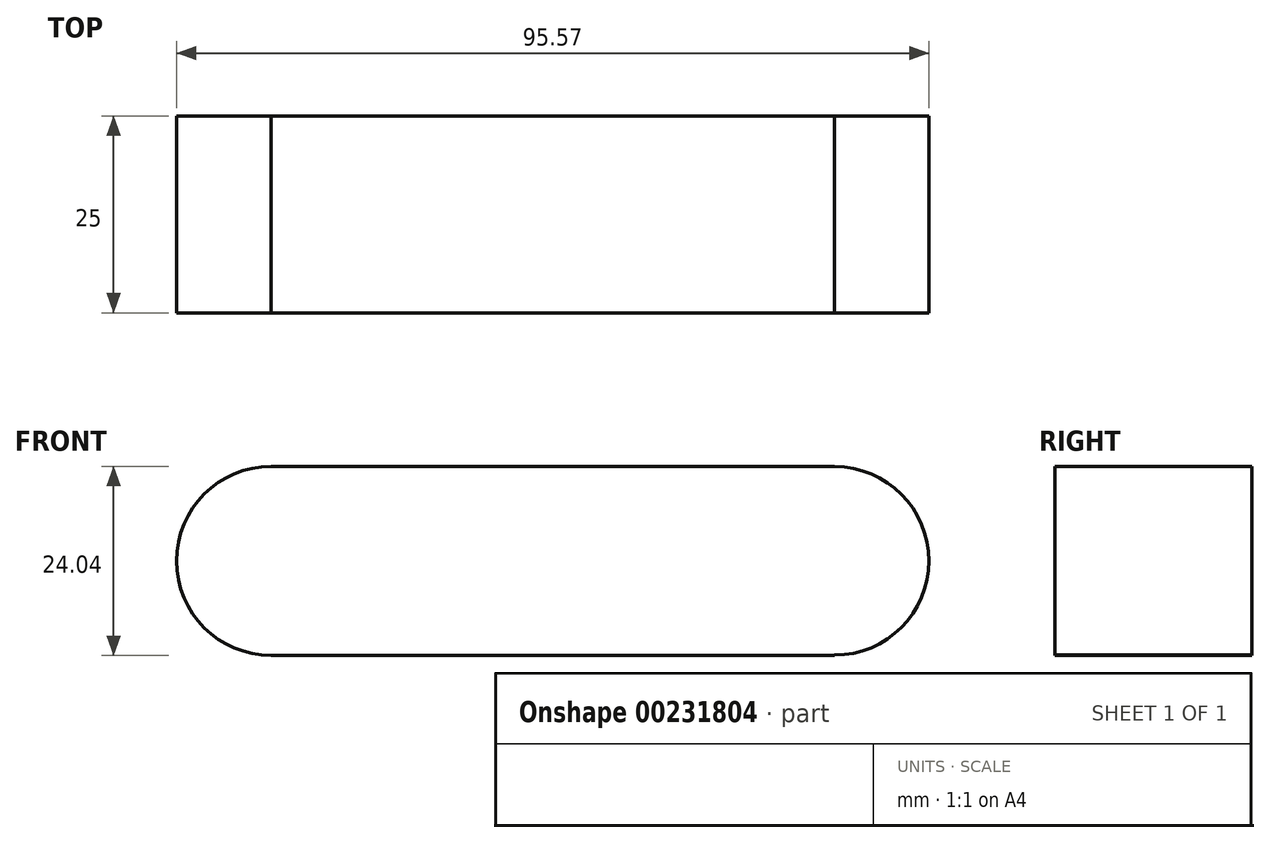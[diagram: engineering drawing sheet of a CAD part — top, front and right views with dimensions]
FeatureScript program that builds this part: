
annotation { "Feature Type Name" : "Feature", "Feature Type Description" : "" }
export const myFeature = defineFeature(function(context is Context, id is Id, definition is map)
    precondition{}
    {
        {
            var Q0;
            Q0=qCreatedBy(makeId("Front.planeOp"),FACE);
            var sketch = newSketch(context, id + "F0", { "sketchPlane" : qUnion([Q0])});
            skLineSegment(sketch, "E0.bottom", {"start": v(-35.8, 12.02) * mm, "end": v(35.8, 12.02) * mm});
            skLineSegment(sketch, "E0.top", {"start": v(-35.8, -12.02) * mm, "end": v(35.8, -12.02) * mm});
            skLineSegment(sketch, "E0.left", {"start": v(-35.8, 12.02) * mm, "end": v(-35.8, -12.02) * mm});
            skLineSegment(sketch, "E0.right", {"start": v(35.8, 12.02) * mm, "end": v(35.8, -12.02) * mm});
            skPoint(sketch, "E0.middle", {"position": v(0, 0) * mm});
            skArc(sketch, "E1", {"start": v(-35.8, 12) * mm, "mid": v(-47.8, 0) * mm, "end": v(-35.8, -12) * mm});
            skArc(sketch, "E2", {"start": v(35.8, -11.97) * mm, "mid": v(47.77, 0) * mm, "end": v(35.8, 11.97) * mm});
            skLineSegment(sketch, "E3", {"start": v(35.8, -12.02) * mm, "end": v(35.8, 12.02) * mm});
            skSolve(sketch);
        }
        {
            var Q0;
            {var subQ0=sQuery(id+"F0.wireOp",EDGE,"E1");Q0=makeQuery(id+"F0.imprint","IMPRINT",FACE,{"disambiguationData":[TD([[makeQuery(id+"F0.imprint","IMPRINT",EDGE,{"derivedFrom":subQ0}),1.0]])]});}
            var Q1;
            {var subQ4=sQuery(id+"F0.wireOp",EDGE,"E0.bottom");Q1=makeQuery(id+"F0.imprint","IMPRINT",FACE,{"disambiguationData":[TD([[makeQuery(id+"F0.imprint","IMPRINT",EDGE,{"derivedFrom":subQ4}),-1.0]])]});}
            var Q2;
            {var subQ0=sQuery(id+"F0.wireOp",EDGE,"E2");Q2=makeQuery(id+"F0.imprint","IMPRINT",FACE,{"disambiguationData":[TD([[makeQuery(id+"F0.imprint","IMPRINT",EDGE,{"derivedFrom":subQ0}),1.0]])]});}
            extrude(context, id + "F1", {"entities" : qUnion([Q0, Q1, Q2]), "depth" : 25 * mm});
        }
    });
